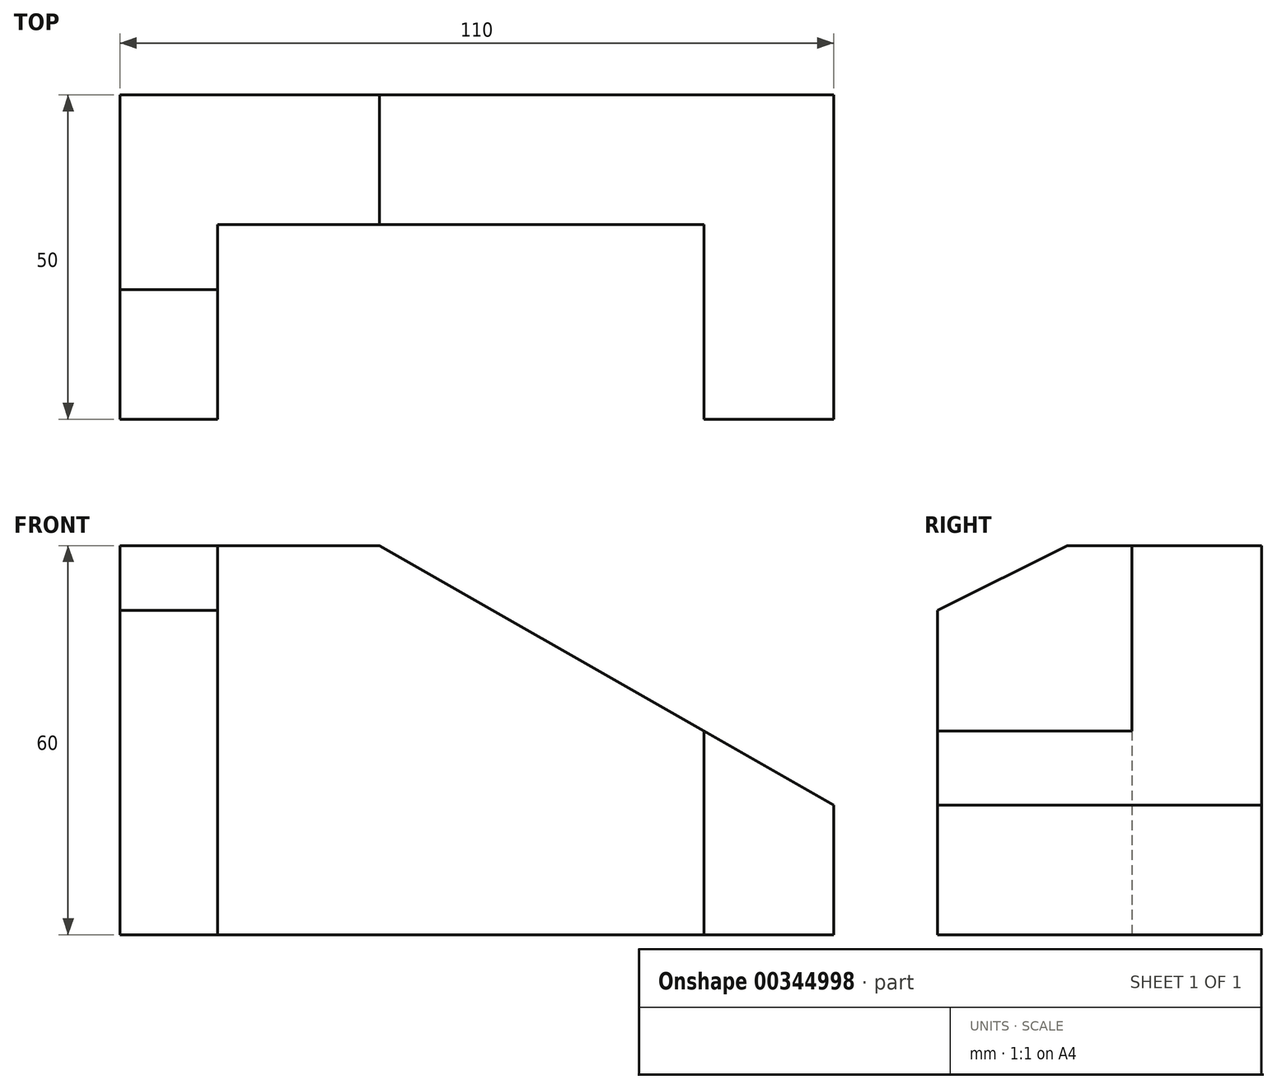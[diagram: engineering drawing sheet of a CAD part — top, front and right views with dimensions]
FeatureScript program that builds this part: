
annotation { "Feature Type Name" : "Feature", "Feature Type Description" : "" }
export const myFeature = defineFeature(function(context is Context, id is Id, definition is map)
    precondition{}
    {
        {
            var Q0;
            Q0=qCreatedBy(makeId("Top.planeOp"),FACE);
            var sketch = newSketch(context, id + "F0", { "sketchPlane" : qUnion([Q0])});
            skLineSegment(sketch, "E0.bottom", {"start": v(-55, 25) * mm, "end": v(55, 25) * mm});
            skLineSegment(sketch, "E0.top", {"start": v(-55, -25) * mm, "end": v(55, -25) * mm});
            skLineSegment(sketch, "E0.left", {"start": v(-55, 25) * mm, "end": v(-55, -25) * mm});
            skLineSegment(sketch, "E0.right", {"start": v(55, 25) * mm, "end": v(55, -25) * mm});
            skPoint(sketch, "E0.middle", {"position": v(0, 0) * mm});
            skLineSegment(sketch, "E1", {"start": v(-55, -25) * mm, "end": v(-40, -25) * mm});
            skLineSegment(sketch, "E2", {"start": v(55, -25) * mm, "end": v(35, -25) * mm});
            skLineSegment(sketch, "E3", {"start": v(-40, -25) * mm, "end": v(-40, 5) * mm});
            skLineSegment(sketch, "E4", {"start": v(35, -25) * mm, "end": v(35, 5) * mm});
            skLineSegment(sketch, "E5", {"start": v(-40, 5) * mm, "end": v(35, 5) * mm});
            skSolve(sketch);
        }
        {
            var Q0;
            Q0=makeQuery(id+"F0.imprint","IMPRINT",FACE,{"disambiguationData":[TD([[makeQuery(id+"F0.imprint","IMPRINT",EDGE,{"derivedFrom":sQuery(id+"F0.wireOp",EDGE,"E0.bottom")}),-1.0]])]});
            extrude(context, id + "F1", {"entities" : qUnion([Q0]), "depth" : 60 * mm});
        }
        {
            var Q0;
            Q0=makeQuery(id+"F1.opExtrude","SWEPT_FACE",FACE,{"disambiguationData":[OSD([sQuery(id+"F0.wireOp",EDGE,"E0.left")])]});
            var sketch = newSketch(context, id + "F2", { "sketchPlane" : qUnion([Q0])});
            skLineSegment(sketch, "E6", {"start": v(5, 60) * mm, "end": v(25, 50) * mm});
            skSolve(sketch);
        }
        {
            var Q0;
            Q0=makeQuery(id+"F2.imprint","IMPRINT",FACE,{"disambiguationData":[TD([[makeQuery(id+"F2.imprint","IMPRINT",EDGE,{"derivedFrom":sQuery(id+"F2.wireOp",EDGE,"aqJsBB5z-QlOF-932Y-Ntzc-XjwIaK7K1Ak8")}),-1.0]])]});
            var Q1;
            {var subQ0=sQuery(id+"F2.wireOp",EDGE,"3uv440IB-Jx05-Nptq-sbQv-D6uVZgrVOvba");Q1=makeQuery(id+"F2.imprint","IMPRINT",FACE,{"disambiguationData":[TD([[makeQuery(id+"F2.imprint","IMPRINT",EDGE,{"derivedFrom":subQ0}),-1.0]])]});}
            var Q2;
            {var subQ0=sQuery(id+"F2.wireOp",EDGE,"E6");Q2=makeQuery(id+"F2.imprint","IMPRINT",FACE,{"disambiguationData":[TD([[makeQuery(id+"F2.imprint","IMPRINT",EDGE,{"derivedFrom":subQ0}),1.0]])]});}
            extrude(context, id + "F3", {"entities" : qUnion([Q0, Q1, Q2]), "operationType" : NewBodyOperationType.REMOVE, "oppositeDirection" : true, "depth" : 15 * mm});
        }
        {
            var Q0;
            Q0=makeQuery(id+"F1.opExtrude","SWEPT_FACE",FACE,{"disambiguationData":[OSD([sQuery(id+"F0.wireOp",EDGE,"E0.bottom")])]});
            var sketch = newSketch(context, id + "F4", { "sketchPlane" : qUnion([Q0])});
            skLineSegment(sketch, "E7", {"start": v(-55, 60) * mm, "end": v(15, 60) * mm});
            skLineSegment(sketch, "E8", {"start": v(-55, 60) * mm, "end": v(-55, 20) * mm});
            skLineSegment(sketch, "E9", {"start": v(-55, 20) * mm, "end": v(15, 60) * mm});
            skSolve(sketch);
        }
        {
            var Q0;
            Q0=makeQuery(id+"F4.imprint","IMPRINT",FACE,{"disambiguationData":[TD([[makeQuery(id+"F4.imprint","IMPRINT",EDGE,{"derivedFrom":sQuery(id+"F4.wireOp",EDGE,"E7")}),1.0]])]});
            extrude(context, id + "F5", {"entities" : qUnion([Q0]), "operationType" : NewBodyOperationType.REMOVE, "oppositeDirection" : true, "depth" : 60 * mm});
        }
    });
